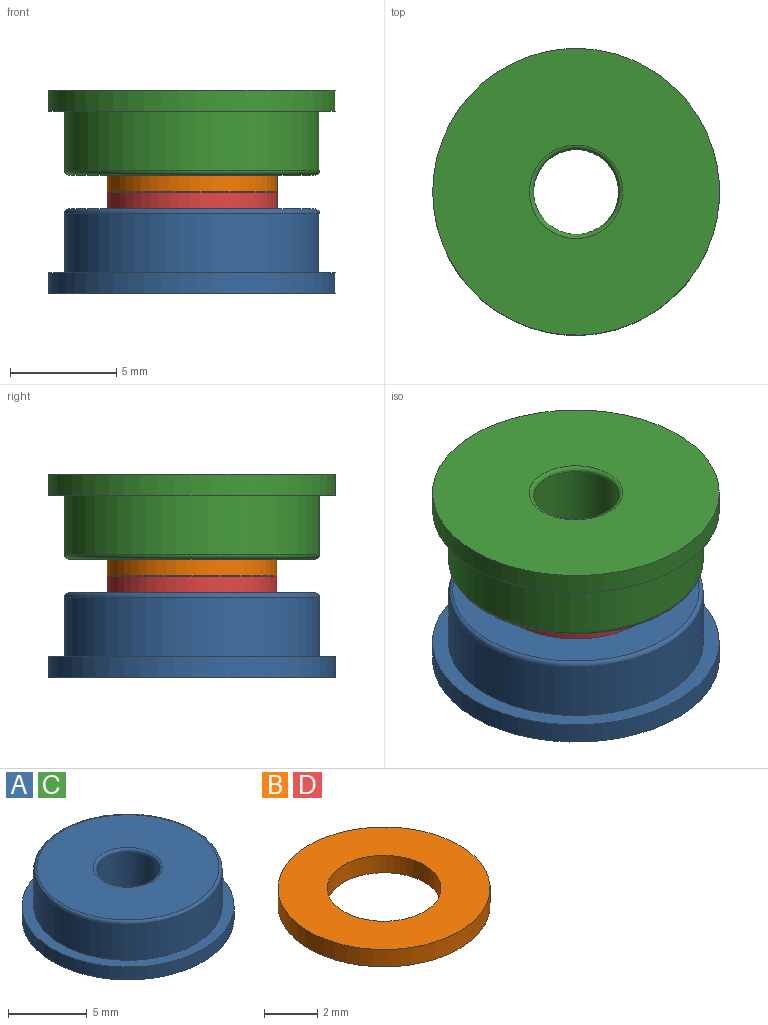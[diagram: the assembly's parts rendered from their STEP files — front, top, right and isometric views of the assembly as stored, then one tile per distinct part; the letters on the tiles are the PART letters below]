
ASSEMBLY  parts=4 mates=3
PART A: 9 faces, bbox 13.5x13.5x4 mm
  f0: plane 13.5x13.5mm, normal (0,0,-1), area 127.9mm2, adj f1,f8
  f1: cylinder r=6.75mm len=13.5mm, axis (0,0,-1), area 42.4mm2, adj f0,f2
  f2: plane 13.5x13.5mm, normal (0,0,1), area 30mm2, adj f1,f3
  f3: cylinder r=6mm len=12mm, axis (0,0,-1), area 105.6mm2, adj f2,f6
  f4: plane 11.6x11.6mm, normal (0,0,1), area 90.5mm2, adj f6,f7
  f5: cylinder r=2mm len=4mm, axis (0,0,-1), area 45.2mm2, adj f7,f8
  f6: torus R=5.8mm, axis (0,0,-1), area 11.7mm2, adj f3,f4
  f7: torus R=2.2mm, axis (0,0,-1), area 4.1mm2, adj f4,f5
  f8: torus R=2.2mm, axis (0,0,1), area 4.1mm2, adj f0,f5
PART B: 4 faces, bbox 8x8x0.8 mm
  f0: cylinder r=2.15mm len=4.3mm, axis (0,0,1), area 10.8mm2, adj f1,f3
  f1: plane 8x8mm, normal (0,0,-1), area 35.7mm2, adj f0,f2
  f2: cylinder r=4mm len=8mm, axis (0,0,1), area 20.1mm2, adj f1,f3
  f3: plane 8x8mm, normal (0,0,1), area 35.7mm2, adj f0,f2
PART C: same geometry as A
PART D: same geometry as B
PLACE A t=(-42.1,13.83,48.91)mm
PLACE B t=(-13.7,13.83,47.68)mm
PLACE C rot(axis=(1,0,0),180deg) t=(-42.1,13.83,58.51)mm
PLACE D rot(axis=(1,0,0),180deg) t=(-13.7,13.83,59.74)mm
MATE fastened D.f0 <-> A.f8  axis (0,0,-1) through (-42.1,13.83,52.91)mm
MATE fastened D.f0 <-> B.f0  axis (0,0,1) through (-42.1,13.83,53.71)mm
MATE fastened C.f1 <-> A.f8  axis (0,0,-1) through (-42.1,13.83,54.51)mm
